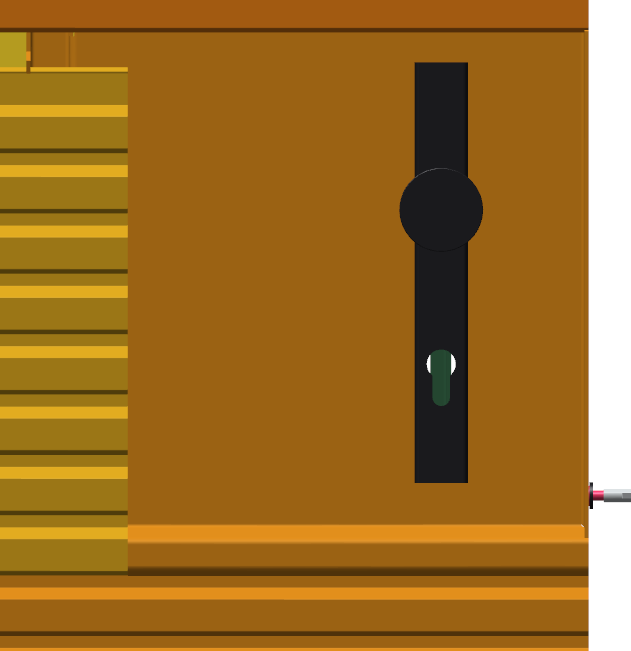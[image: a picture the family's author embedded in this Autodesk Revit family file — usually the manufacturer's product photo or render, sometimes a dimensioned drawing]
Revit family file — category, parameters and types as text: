
# Revit family: NLRS_31_DO_WB_HJ44 dubbele deur-AV_jazo_jazo
name_source: partatom
category: Doors
units: mm (PartAtom-declared; Revit-internal decimal feet)

## family parameters
Always vertical = Yes
Cut with Voids When Loaded = No
Host = Wall
OmniClass Number = 23.30.10.00
OmniClass Title = Doors
Room Calculation Point = No
Shared = No

## types (1)
- TYPE CATALOG
    Analytic Construction = <None>
    Assembly Code = 23.30.10.00
    Construction Type = Voor specificaties of mogelijkheden, neem contact op.
    Define Thermal Properties by = User Defined
    Description = HJ44 dubbele deur
    Function = Exterior
    Height = 2000 mm  [stored 6.56168 ft]
    JAZO_C_aluminium kozijn = No
    JAZO_C_breedte_loopdeur = 1000 mm  [stored 3.28084 ft]
    JAZO_C_breedte_vaste deur = 1000 mm  [stored 3.28084 ft]
    JAZO_C_calculatie_01 = 37 mm  [stored 0.121391 ft]
    JAZO_C_calculatie_02 = 565 mm
    JAZO_C_calculatie_03 = -59 mm
    JAZO_C_dagmaat loopdeur breedte = 915 mm
    JAZO_C_dagmaat loopdeur hoogte = 1915 mm
    JAZO_C_forster presto kozijn = Yes
    JAZO_C_materiaal aluminium kozijn = <By Category>
    JAZO_C_materiaal aluminium planken = <By Category>
    JAZO_C_materiaal beslag = <By Category>
    JAZO_C_materiaal forster presto deurprofiel = <By Category>
    JAZO_C_materiaal forster presto kozijn = <By Category>
    JAZO_C_materiaal forster presto sandwichpaneel = <By Category>
    JAZO_C_materiaal scharnier = <By Category>
    JAZO_C_materiaal schoep = <By Category>
    JAZO_C_niet ventilerend = Yes
    JAZO_C_opbouwrooster HJ44 = Yes
    JAZO_C_paniekfunctie = No
    JAZO_C_ventilerend = No
    MAX HEIGHT = 3000 mm  [stored 9.84252 ft]
    MAX WIDTH = 2890 mm
    MIN HEIGHT = 1850 mm  [stored 6.06955 ft]
    MIN WIDTH = 1400 mm  [stored 4.59318 ft]
    Manufacturer = JAZO Zevenaar bv
    Model = HJ44 dubbele deur
    NLRS_C_aantal_01 = 2
    NLRS_C_aantal_02 = 11
    NLRS_C_brandwerend = No
    NLRS_C_breedte = 2000 mm  [stored 6.56168 ft]
    NLRS_C_breedte_01 = 2010 mm  [stored 6.59449 ft]
    NLRS_C_breedte_02 = 1000 mm  [stored 3.28084 ft]
    NLRS_C_breedte_03 = 1000 mm  [stored 3.28084 ft]
    NLRS_C_breedte_max = 2890 mm
    NLRS_C_breedte_min = 1400 mm  [stored 4.59318 ft]
    NLRS_C_content_datum gewijzigd = 7-11-2022
    NLRS_C_content_datum uitgifte = 22-8-2022
    NLRS_C_content_provider = JAZO Zevenaar bv
    NLRS_C_content_revit versie = REVIT 2020.2
    NLRS_C_content_versie = 2.5
    NLRS_C_diepte = 50 mm  [stored 0.164042 ft]
    NLRS_C_diepte_01 = 111 mm
    NLRS_C_diepte_02 = 50 mm  [stored 0.164042 ft]
    NLRS_C_geluidwering Rw = Voor specificaties of mogelijkheden, neem contact op.
    NLRS_C_hoogte = 2000 mm  [stored 6.56168 ft]
    NLRS_C_hoogte_01 = 2010 mm  [stored 6.59449 ft]
    NLRS_C_hoogte_max = 3000 mm  [stored 9.84252 ft]
    NLRS_C_hoogte_min = 1850 mm  [stored 6.06955 ft]
    NLRS_C_inbraakwerend = No
    NLRS_C_lengte_01 = 96 mm  [stored 0.314961 ft]
    NLRS_C_lengte_02 = 565 mm
    NLRS_C_leverancier_adres = Handelsdwarsstraat 10
    NLRS_C_leverancier_bedrijfsnaam = JAZO Zevenaar bv
    NLRS_C_leverancier_plaats = Zevenaar
    NLRS_C_leverancier_postcode = 6905 DJ
    NLRS_C_leverancier_telefoonnummer = +31 316 - 59 29 11
    NLRS_C_leverancier_url = www.jazo.com
    NLRS_C_merk = Voor specificaties of mogelijkheden, neem contact op.
    NLRS_C_offset = 61 mm
    NLRS_C_offset_01 = 0 mm  [stored 0 ft]
    NLRS_C_offset_02 = 37 mm  [stored 0.121391 ft]
    NLRS_C_rookwerendheid = Voor specificaties of mogelijkheden, neem contact op.
    NLRS_C_stelruimte = 5 mm  [stored 0.0164042 ft]
    NLRS_C_vluchtroute = Voor specificaties of mogelijkheden, neem contact op.
    NLRS_C_weerstandsklasse = Voor specificaties of mogelijkheden, neem contact op.
    NLRS_C_zelfsluitend = No
    Negge = 61 mm
    Rough Height = 2010 mm  [stored 6.59449 ft]
    Rough Width = 2010 mm  [stored 6.59449 ft]
    Thickness = 50 mm  [stored 0.164042 ft]
    URL = www.jazo.com
    Wall Closure = By host
    Width = 2000 mm  [stored 6.56168 ft]

note: [stored X ft] marks values corroborated as IEEE doubles in the binary element streams (Revit-internal decimal feet)

## geometry (parser evidence)
native form markers: Sweep x59
no freeform markers — native parametric forms only
